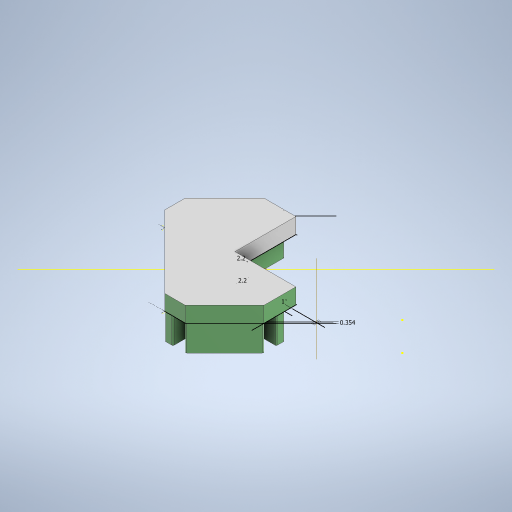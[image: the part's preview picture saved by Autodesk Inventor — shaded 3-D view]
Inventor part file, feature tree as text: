
AUTODESK INVENTOR PART (.ipt)
format: ipt  version: 2023 (Build 270158000, 158)  size: 378,368 bytes
history: native  units: in
note: dims shown in document units (in); Inventor stores cm internally (conversion verified against a paired STEP export)
features: other x5, sketch x2, plane x1, mirror x1, extrude x1
ambient origin geometry x8: Origin, YZ Plane, XZ Plane, XY Plane, X Axis, Y Axis, Z Axis, Center Point
bodies: Body1 (feature_tree)
feature tree (10):
  other  "TmpPart3.ipt"
  plane  "Work Plane1"
  mirror  "Mirror1"
  extrude  "Extrusion1"  [1 undecoded]
  other  "Work Axis1"
  other  "PLA2::TmpPart3.ipt"
  other  "TaggingFeature1"
  sketch  "Sketch1"  dims[d0=0.3937in d1=-0.5011in]
  sketch  "Sketch2"  dims[d2=0.1181in d3=0.0in d4=0.0866in d5=0.0866in d8=0.0394in d9=0.0139in]
  other  "PLA2"
note: 1 required parameter value undecoded (feature->parameter linkage not recoverable at this tier; creation-order binding heuristic only, values carry confidence <= 0.55)
